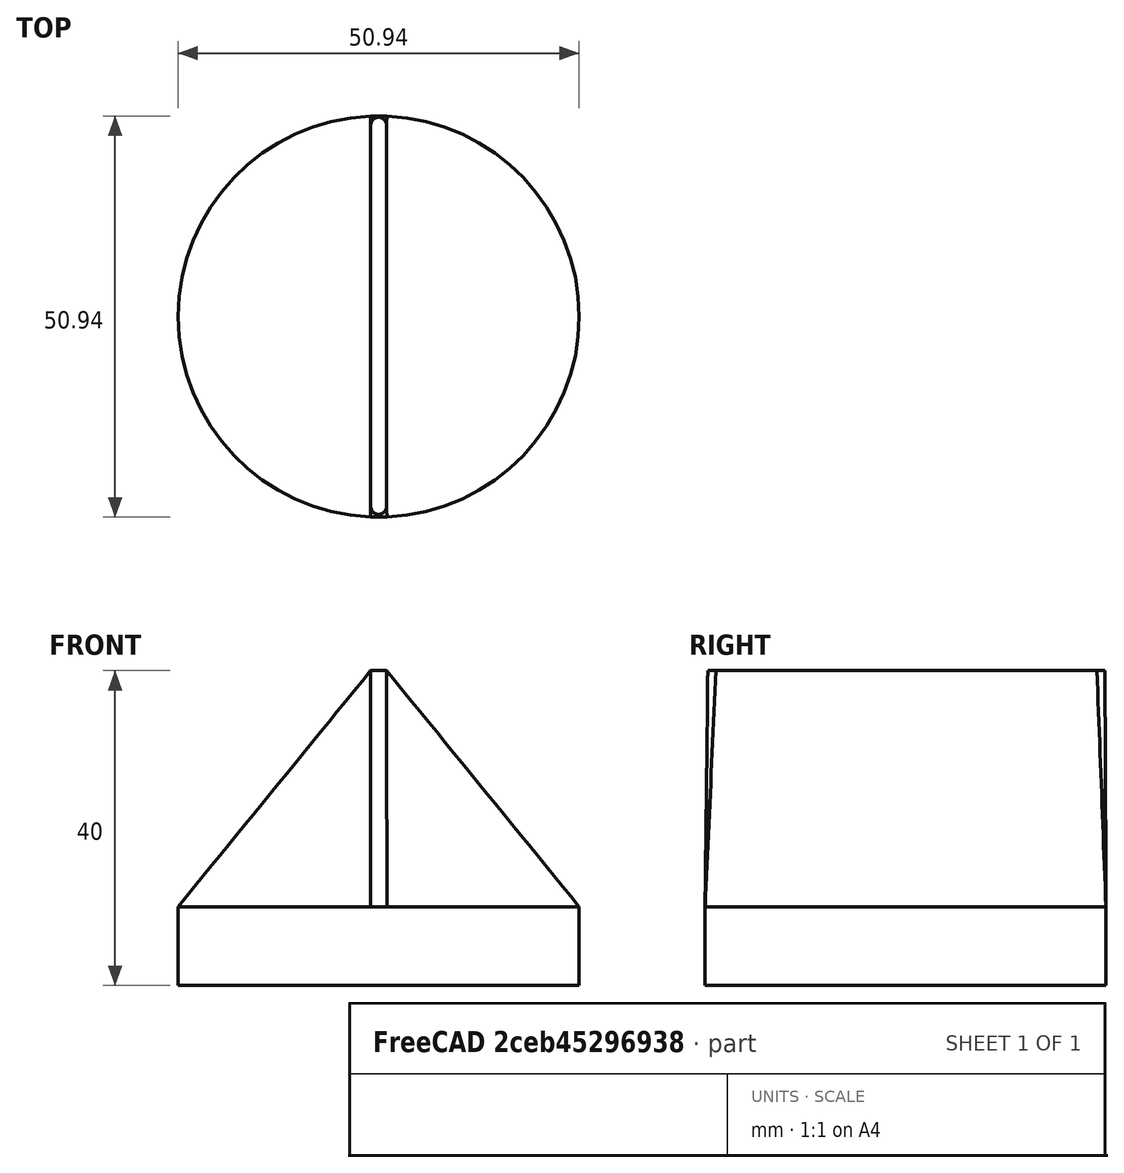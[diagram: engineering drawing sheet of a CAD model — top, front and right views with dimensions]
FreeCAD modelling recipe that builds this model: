
FCSTD DOCUMENT  (FreeCAD 1.2R20251230 (Git shallow))
Label: loft_2
License: All rights reserved
LicenseURL: https://en.wikipedia.org/wiki/All_rights_reserved
objects: Sketcher::SketchObject×2, App::Point×1, PartDesign::Pad×1, PartDesign::AdditiveLoft×1, PartDesign::Body×1
note: 11 computed .brp shape members not serialized (recipe doc carries the construction recipe); baked Part::Feature solids carry a one-line shape summary decoded from their .brp

FEATURE [App::Point] Origin001
  Role = Origin
FEATURE [Sketcher::SketchObject] Sketch
  ArcFitTolerance = 1e-06
  AttachmentSupport = -> [Origin]
  ExternalTypes = [0]
  FullyConstrained = false
  MakeInternals = false
  MapMode = 5
  sketch-geometry (1):
    g0: Circle CenterX=0 CenterY=0 CenterZ=0 NormalX=0 NormalY=0 NormalZ=1 AngleXU=0 Radius=25.4736
  constraints (1):
    c: Coincident(g0,g-1)
FEATURE [PartDesign::Pad] Pad
  Direction = (0,0,1)
  Length = 10
  Length2 = 10
  Profile = -> Sketch
  ReferenceAxis = -> Sketch [N_Axis]
  Refine = true
  Reversed = true
  SideType = 0
  Suppressed = false
  Type = 0
  Type2 = 0
FEATURE [Sketcher::SketchObject] Sketch001
  ArcFitTolerance = 1e-06
  AttachmentOffset = pos=(0,0,30) rot=(0,0,1;0rad)
  AttachmentSupport = -> [Origin]
  ExternalTypes = [0]
  FullyConstrained = false
  MakeInternals = false
  MapMode = 5
  Placement = pos=(0,0,30) rot=(0,0,1;0rad)
  sketch-geometry (4):
    g0: ArcOfCircle CenterX=0 CenterY=24.3069 CenterZ=0 NormalX=0 NormalY=0 NormalZ=1 AngleXU=0 Radius=1.00511 StartAngle=9e-16 EndAngle=3.14159
    g1: ArcOfCircle CenterX=0 CenterY=-24.1154 CenterZ=0 NormalX=0 NormalY=0 NormalZ=1 AngleXU=0 Radius=1.00511 StartAngle=3.14159 EndAngle=6.28319
    g2: LineSegment StartX=1.00511 StartY=24.3069 StartZ=0 EndX=1.00511 EndY=-24.1154 EndZ=0
    g3: LineSegment StartX=-1.00511 StartY=24.3069 StartZ=0 EndX=-1.00511 EndY=-24.1154 EndZ=0
  constraints (7):
    c: Tangent(g0,g2) = 1.5708
    c: Tangent(g0,g3) = -1.5708
    c: Tangent(g1,g2) = 1.5708
    c: Tangent(g1,g3) = -1.5708
    c: Equal(g0,g1)
    c: PointOnObject(g0,g-2)
    c: PointOnObject(g1,g-2)
FEATURE [PartDesign::AdditiveLoft] AdditiveLoft
  BaseFeature = -> Pad
  Closed = false
  Profile = -> Pad [Face2]
  Refine = true
  Ruled = false
  Sections = -> [Sketch001]
  Suppressed = false
FEATURE [PartDesign::Body] Body
  AllowCompound = false
  Group = -> [Sketch,Pad,Sketch001,AdditiveLoft]
  Origin = -> Origin
  Tip = -> AdditiveLoft
